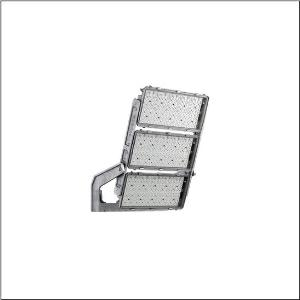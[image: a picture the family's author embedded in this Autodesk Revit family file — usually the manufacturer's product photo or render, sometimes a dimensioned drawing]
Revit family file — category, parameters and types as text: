
# Revit family: floodlight_fl_11_maxi_pro_remote___pl43_5xa779427a01ba_e28e
name_source: partatom
category: Lighting Fixtures
units: mm (PartAtom-declared; Revit-internal decimal feet)

## family parameters
Cut with Voids When Loaded = No
Host = Face
Light Source = No
Part Type = Normal
Room Calculation Point = No
Round Connector Dimension = Use Diameter
Shared = No

## types (1)
- --- (1 x LED, 151320 lm, 1095.9 W, 5000K)
    Apparent Load = 1096 VA
    CIE Flux Codes = 25 74 99 100 100
    Color Rendering = 70
    Color Temperature = 5000K
    Default Elevation = 1800 mm
    Description = Floodlight FL 11  maxi  pro Remote floodlight; light control with lens of PMMA; cover panel of toughened safety glass, transparent; light distribution: PL43, asymmetric direct distribution, LEDcolour temperature: 5000K, rated luminous flux: 151.320lm, colour rendering: CRI > 70, light colour: 750; luminous efficacy: 138lm/W; brightness control: DALI 2 (1 DALI address); with terminal, 8-pole, max. 2.5mm², mains connection: 220..240V/380..400V AC, 50/60Hz, surge voltage resistance: line to ground: 10kV, ECG replaceable separately, no afterglow with DALI off / DMX off command, LED unit replaceable without ESD environment, dustproof LED module, dimming range 10..100%; 1096W floodlight with 2x LED unit of diecast aluminium, coated grey; length: 713mm / width: 651mm / height: 338mm; mounting bracket, of diecast aluminium, uncoated, natural, equipment: Power, protection rating (complete): IP66; insulation class (complete): insulation class I (protective earthing); certification: CE, ENEC, VDE; ball protection: ball impact resistance with accessories, impact resistance: IK07; only for outdoor installations, rated ambient temperature 10°C, permissible operating ambient temperature: -40..+30°C, permissible storage temperature: -40..+85°C; packaging unit: 1 piece

Light Distribution: PL43
    Height = 320 mm
    Lamp = 1 x LED
    Lamp Light Flux = 151320 lm
    Lamp Power = 1095.9 W
    Lamp count = 1
    Length = 1002 mm
    Luminous efficacy = 138 lm/W
    Manufacturer = Siteco
    ModVariant = No
    Model = 5XA779427A01BA
    Mounting Place = Ceiling
    Mounting Type = Surface mounted
    Number of Poles = 1
    OnlyDefault = Yes
    Power Factor = 1
    Product Name = Floodlight FL 11 maxi pro Remote | PL43
    Product group = floodlight | ceiling mounted
    ProductGroupID = 303
    Protection Class = Protection class I
    Protection Degree = IP 66
    RLX_Detail_Level = 1
    RLX_Emergency_Light_Flux = 0 lm
    RLX_Emergency_Type = 0
    RLX_Emergency_Type_DB = No
    RlxData = <blob elided: 52569 chars, md5=6cdef944>
    Socket = socket
    Standby Power = 0 W
    System Light Flux = 151320 lm
    System Power = 1096 W
    Type Comments = factory setting: luminous flux: 100 % | dim-lin: 254 | 760 mA
    Type Image = l_1006784.jpg
    URL = http://relux.com
    VarID = @adj_044921
    Voltage = 0 V
    Weight = 0.00 kg
    Width = 655 mm

## geometry (parser evidence)
native form markers: Blend x4, Sweep x13
no freeform markers — native parametric forms only
